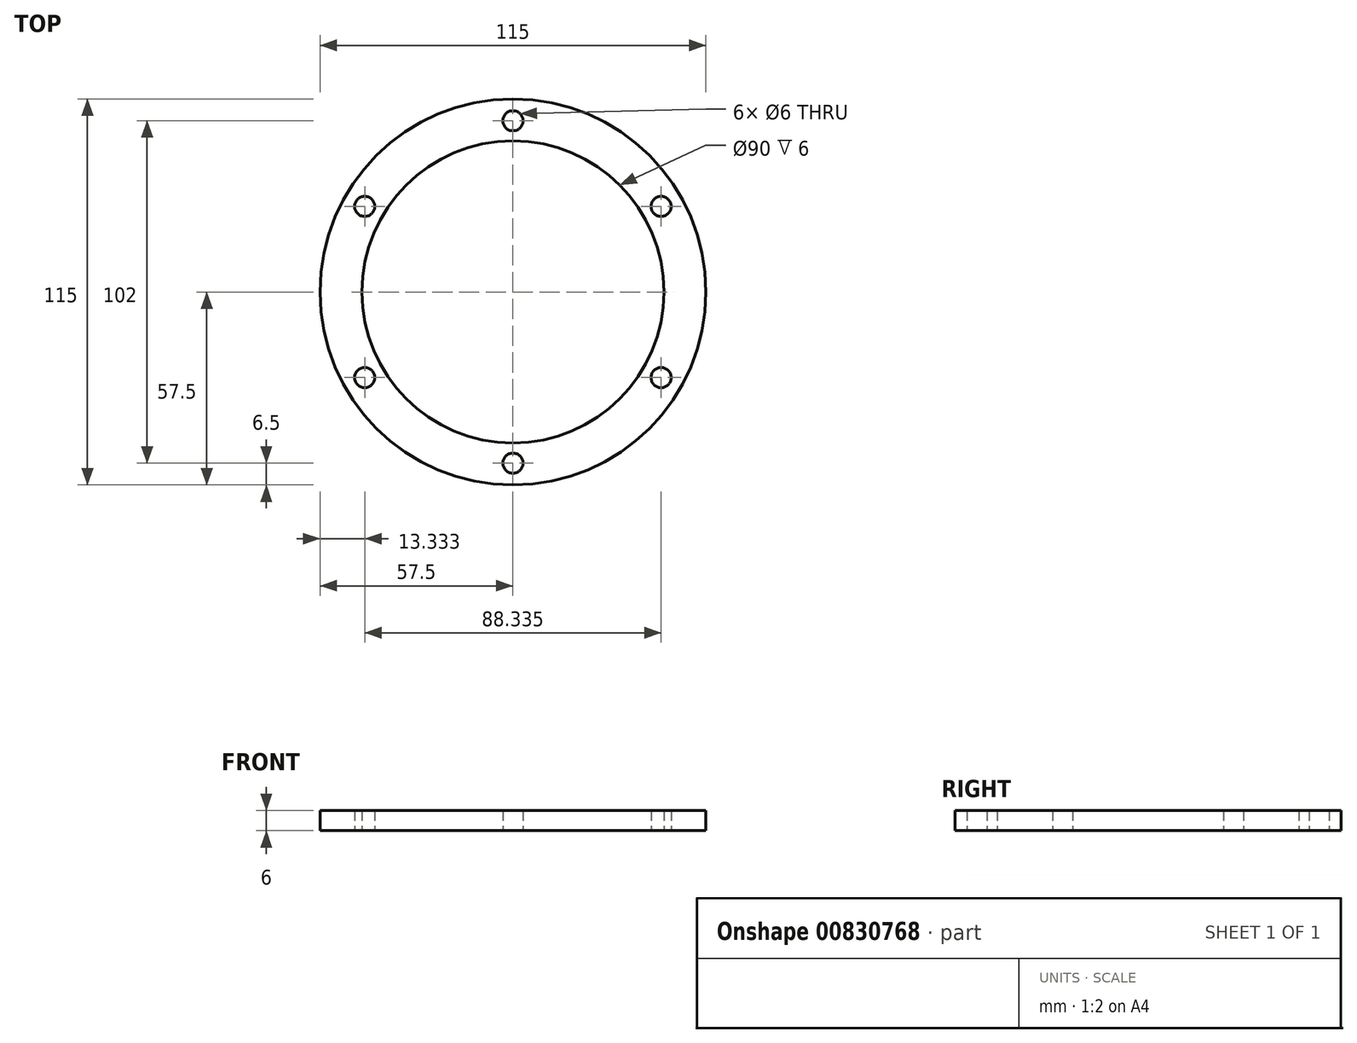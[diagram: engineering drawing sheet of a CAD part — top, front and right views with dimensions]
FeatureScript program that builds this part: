
annotation { "Feature Type Name" : "Feature", "Feature Type Description" : "" }
export const myFeature = defineFeature(function(context is Context, id is Id, definition is map)
    precondition{}
    {
        {
            var Q0;
            Q0=qCreatedBy(makeId("Top.planeOp"),FACE);
            var sketch = newSketch(context, id + "F0", { "sketchPlane" : qUnion([Q0])});
            skCircle(sketch, "E0", {"center": v(0, 0) * mm, "radius": 45 * mm});
            skCircle(sketch, "E1", {"center": v(0, 0) * mm, "radius": 57.5 * mm});
            skCircle(sketch, "E2", {"center": v(0, 51) * mm, "radius": 3 * mm});
            skCircle(sketch, "E3.1.0", {"center": v(-44.17, 25.5) * mm, "radius": 3 * mm});
            skCircle(sketch, "E3.2.0", {"center": v(-44.17, -25.5) * mm, "radius": 3 * mm});
            skCircle(sketch, "E4.1.3.0", {"center": v(0, -51) * mm, "radius": 3 * mm});
            skCircle(sketch, "E4.1.4.0", {"center": v(44.17, -25.5) * mm, "radius": 3 * mm});
            skCircle(sketch, "E4.1.5.0", {"center": v(44.17, 25.5) * mm, "radius": 3 * mm});
            skSolve(sketch);
        }
        {
            var Q0;
            Q0=makeQuery(id+"F0.imprint","IMPRINT",FACE,{"disambiguationData":[TD([[makeQuery(id+"F0.imprint","IMPRINT",EDGE,{"derivedFrom":sQuery(id+"F0.wireOp",EDGE,"E0")}),-1.0]])]});
            extrude(context, id + "F1", {"entities" : qUnion([Q0]), "depth" : 6 * mm, "offsetDistance" : 25 * mm});
        }
    });
